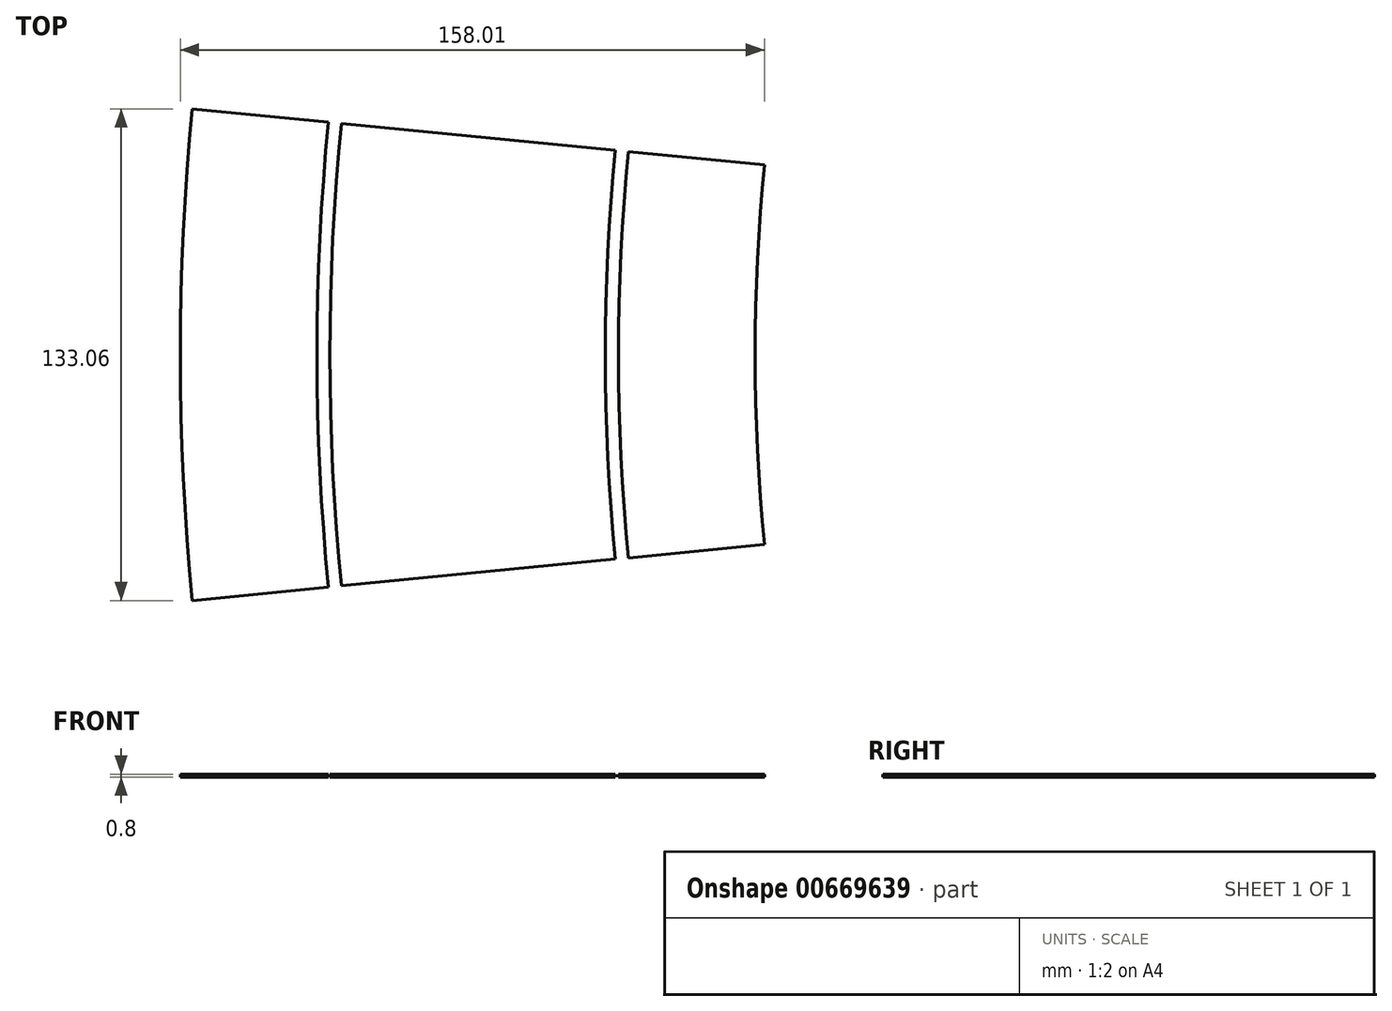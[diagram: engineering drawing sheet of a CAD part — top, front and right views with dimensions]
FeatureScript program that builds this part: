
annotation { "Feature Type Name" : "Feature", "Feature Type Description" : "" }
export const myFeature = defineFeature(function(context is Context, id is Id, definition is map)
    precondition{}
    {
        {
            var Q0;
            Q0=qCreatedBy(makeId("Front.planeOp"),FACE);
            var sketch = newSketch(context, id + "F0", { "sketchPlane" : qUnion([Q0])});
            skLineSegment(sketch, "E0.bottom", {"start": v(0.25, 0) * mm, "end": v(37.25, 0) * mm});
            skLineSegment(sketch, "E0.top", {"start": v(0.25, -0.8) * mm, "end": v(37.25, -0.8) * mm});
            skLineSegment(sketch, "E0.left", {"start": v(0.25, 0) * mm, "end": v(0.25, -0.8) * mm});
            skLineSegment(sketch, "E0.right", {"start": v(37.25, 0) * mm, "end": v(37.25, -0.8) * mm});
            skLineSegment(sketch, "E1.bottom", {"start": v(40.75, 0) * mm, "end": v(115.25, 0) * mm});
            skLineSegment(sketch, "E1.top", {"start": v(40.75, -0.8) * mm, "end": v(115.25, -0.8) * mm});
            skLineSegment(sketch, "E1.left", {"start": v(40.75, 0) * mm, "end": v(40.75, -0.8) * mm});
            skLineSegment(sketch, "E1.right", {"start": v(115.25, 0) * mm, "end": v(115.25, -0.8) * mm});
            skLineSegment(sketch, "E2.bottom", {"start": v(118.75, 0) * mm, "end": v(155.75, 0) * mm});
            skLineSegment(sketch, "E2.top", {"start": v(118.75, -0.8) * mm, "end": v(155.75, -0.8) * mm});
            skLineSegment(sketch, "E2.left", {"start": v(118.75, 0) * mm, "end": v(118.75, -0.8) * mm});
            skLineSegment(sketch, "E2.right", {"start": v(155.75, 0) * mm, "end": v(155.75, -0.8) * mm});
            skLineSegment(sketch, "E3", {"start": v(682, 47.5) * mm, "end": v(682, -34.44) * mm});
            skSolve(sketch);
        }
        {
            var Q0;
            Q0=makeQuery(id+"F0.imprint","IMPRINT",FACE,{"disambiguationData":[TD([[makeQuery(id+"F0.imprint","IMPRINT",EDGE,{"derivedFrom":sQuery(id+"F0.wireOp",EDGE,"E0.bottom")}),-1.0]])]});
            var Q1;
            Q1=makeQuery(id+"F0.imprint","IMPRINT",FACE,{"disambiguationData":[TD([[makeQuery(id+"F0.imprint","IMPRINT",EDGE,{"derivedFrom":sQuery(id+"F0.wireOp",EDGE,"E1.bottom")}),-1.0]])]});
            var Q2;
            Q2=makeQuery(id+"F0.imprint","IMPRINT",FACE,{"disambiguationData":[TD([[makeQuery(id+"F0.imprint","IMPRINT",EDGE,{"derivedFrom":sQuery(id+"F0.wireOp",EDGE,"E2.bottom")}),-1.0]])]});
            var Q3;
            Q3=sQuery(id+"F0.wireOp",EDGE,"E3");
            revolve(context, id + "F1", {"entities" : qUnion([Q0, Q1, Q2]), "axis" : qUnion([Q3]), "revolveType" : RevolveType.SYMMETRIC, "angle" : 11.2 * degree});
        }
    });
